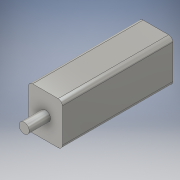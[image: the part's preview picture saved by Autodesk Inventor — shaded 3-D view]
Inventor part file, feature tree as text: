
AUTODESK INVENTOR PART (.ipt)
format: ipt  version: 2016 (Build 200138000, 138)  size: 132,608 bytes
history: native  units: in
note: dims shown in document units (in); Inventor stores cm internally (conversion verified against a paired STEP export)
features: extrude x2, sketch x2, fillet x1
ambient origin geometry x8: Origin, YZ Plane, XZ Plane, XY Plane, X Axis, Y Axis, Z Axis, Center Point
bodies: Solid1 (feature_tree)
feature tree (5):
  extrude  "Extrusion1"  Depth=1.3in
  fillet  "Fillet1"  Radius=0.5in
  extrude  "Extrusion2"  Depth=0.25in
  sketch  "Sketch1"  dims[d0=0.4in d1=1.3in d2=0.5in d3=0.0in]
  sketch  "Sketch2"  dims[d4=0.05in d5=0.12in d6=0.25in d7=0.0in]
